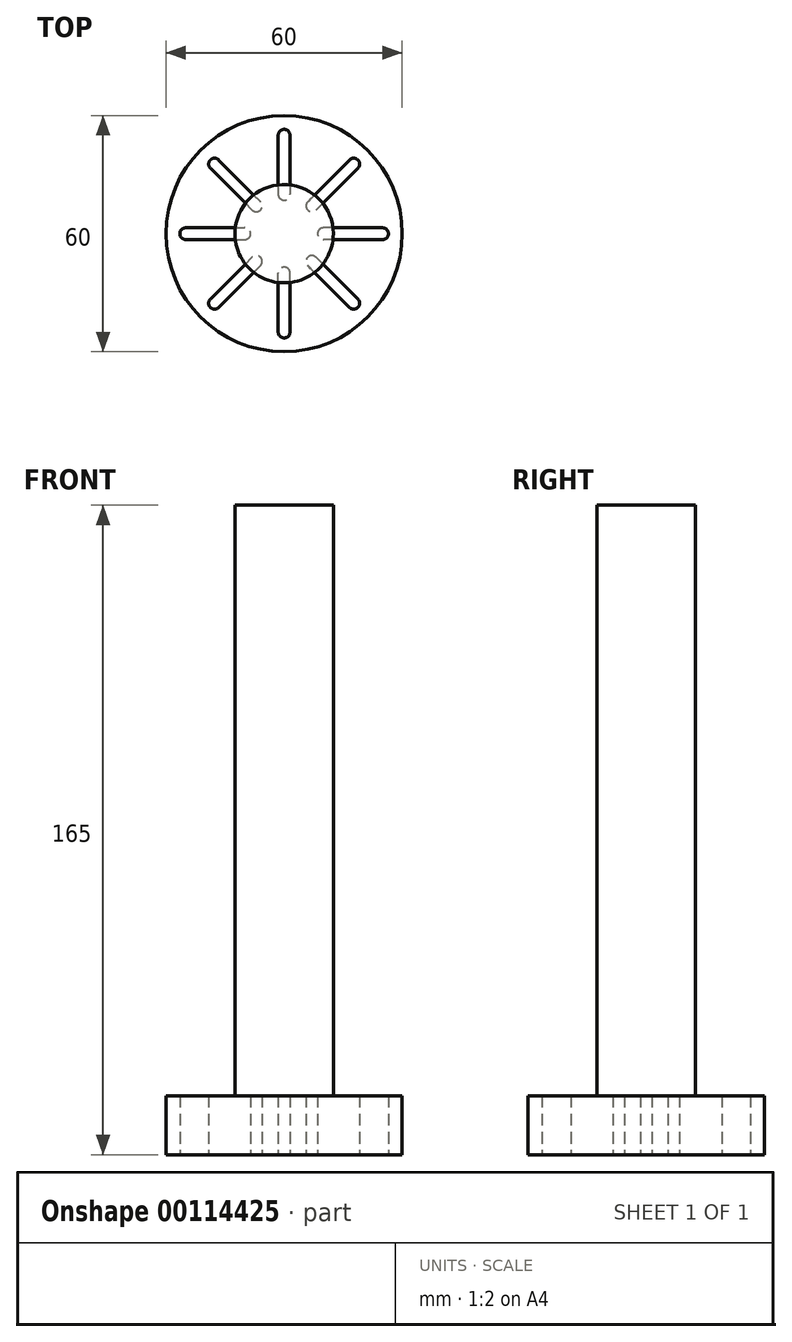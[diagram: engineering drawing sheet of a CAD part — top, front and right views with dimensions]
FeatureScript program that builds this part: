
annotation { "Feature Type Name" : "Feature", "Feature Type Description" : "" }
export const myFeature = defineFeature(function(context is Context, id is Id, definition is map)
    precondition{}
    {
        {
            var Q0;
            Q0=qCreatedBy(makeId("Top.planeOp"),FACE);
            var sketch = newSketch(context, id + "F0", { "sketchPlane" : qUnion([Q0])});
            skCircle(sketch, "E0", {"center": v(0, 0) * mm, "radius": 30 * mm});
            skArc(sketch, "E1", {"start": v(-25, 1.5) * mm, "mid": v(-26.5, 0) * mm, "end": v(-25, -1.5) * mm});
            skLineSegment(sketch, "E2.bottom", {"start": v(-25, 1.5) * mm, "end": v(-10, 1.5) * mm});
            skLineSegment(sketch, "E2.top", {"start": v(-25, -1.5) * mm, "end": v(-10, -1.5) * mm});
            skLineSegment(sketch, "E2.left", {"start": v(-25, 1.5) * mm, "end": v(-25, -1.5) * mm, "construction": true});
            skLineSegment(sketch, "E2.right", {"start": v(-10, 1.5) * mm, "end": v(-10, -1.5) * mm, "construction": true});
            skArc(sketch, "E3", {"start": v(-10, -1.5) * mm, "mid": v(-8.5, 0) * mm, "end": v(-10, 1.5) * mm});
            skLineSegment(sketch, "E4.1.0", {"start": v(-18.74, -16.62) * mm, "end": v(-8.13, -6.01) * mm});
            skLineSegment(sketch, "E4.1.1", {"start": v(-16.62, -18.74) * mm, "end": v(-6.01, -8.13) * mm});
            skArc(sketch, "E4.1.2", {"start": v(-6.01, -8.13) * mm, "mid": v(-6.01, -6.01) * mm, "end": v(-8.13, -6.01) * mm});
            skArc(sketch, "E4.1.3", {"start": v(-18.74, -16.62) * mm, "mid": v(-18.74, -18.74) * mm, "end": v(-16.62, -18.74) * mm});
            skLineSegment(sketch, "E4.2.0", {"start": v(-1.5, -25) * mm, "end": v(-1.5, -10) * mm});
            skLineSegment(sketch, "E4.2.1", {"start": v(1.5, -25) * mm, "end": v(1.5, -10) * mm});
            skArc(sketch, "E4.2.2", {"start": v(1.5, -10) * mm, "mid": v(0, -8.5) * mm, "end": v(-1.5, -10) * mm});
            skArc(sketch, "E4.2.3", {"start": v(-1.5, -25) * mm, "mid": v(0, -26.5) * mm, "end": v(1.5, -25) * mm});
            skLineSegment(sketch, "E4.3.0", {"start": v(16.62, -18.74) * mm, "end": v(6.01, -8.13) * mm});
            skLineSegment(sketch, "E4.3.1", {"start": v(18.74, -16.62) * mm, "end": v(8.13, -6.01) * mm});
            skArc(sketch, "E4.3.2", {"start": v(8.13, -6.01) * mm, "mid": v(6.01, -6.01) * mm, "end": v(6.01, -8.13) * mm});
            skArc(sketch, "E4.3.3", {"start": v(16.62, -18.74) * mm, "mid": v(18.74, -18.74) * mm, "end": v(18.74, -16.62) * mm});
            skLineSegment(sketch, "E4.4.0", {"start": v(25, -1.5) * mm, "end": v(10, -1.5) * mm});
            skLineSegment(sketch, "E4.4.1", {"start": v(25, 1.5) * mm, "end": v(10, 1.5) * mm});
            skArc(sketch, "E4.4.2", {"start": v(10, 1.5) * mm, "mid": v(8.5, 0) * mm, "end": v(10, -1.5) * mm});
            skArc(sketch, "E4.4.3", {"start": v(25, -1.5) * mm, "mid": v(26.5, 0) * mm, "end": v(25, 1.5) * mm});
            skLineSegment(sketch, "E4.5.0", {"start": v(18.74, 16.62) * mm, "end": v(8.13, 6.01) * mm});
            skLineSegment(sketch, "E4.5.1", {"start": v(16.62, 18.74) * mm, "end": v(6.01, 8.13) * mm});
            skArc(sketch, "E4.5.2", {"start": v(6.01, 8.13) * mm, "mid": v(6.01, 6.01) * mm, "end": v(8.13, 6.01) * mm});
            skArc(sketch, "E4.5.3", {"start": v(18.74, 16.62) * mm, "mid": v(18.74, 18.74) * mm, "end": v(16.62, 18.74) * mm});
            skLineSegment(sketch, "E4.6.0", {"start": v(1.5, 25) * mm, "end": v(1.5, 10) * mm});
            skLineSegment(sketch, "E4.6.1", {"start": v(-1.5, 25) * mm, "end": v(-1.5, 10) * mm});
            skArc(sketch, "E4.6.2", {"start": v(-1.5, 10) * mm, "mid": v(0, 8.5) * mm, "end": v(1.5, 10) * mm});
            skArc(sketch, "E4.6.3", {"start": v(1.5, 25) * mm, "mid": v(0, 26.5) * mm, "end": v(-1.5, 25) * mm});
            skLineSegment(sketch, "E4.7.0", {"start": v(-16.62, 18.74) * mm, "end": v(-6.01, 8.13) * mm});
            skLineSegment(sketch, "E4.7.1", {"start": v(-18.74, 16.62) * mm, "end": v(-8.13, 6.01) * mm});
            skArc(sketch, "E4.7.2", {"start": v(-8.13, 6.01) * mm, "mid": v(-6.01, 6.01) * mm, "end": v(-6.01, 8.13) * mm});
            skArc(sketch, "E4.7.3", {"start": v(-16.62, 18.74) * mm, "mid": v(-18.74, 18.74) * mm, "end": v(-18.74, 16.62) * mm});
            skSolve(sketch);
        }
        {
            var Q0;
            Q0=makeQuery(id+"F0.imprint","IMPRINT",FACE,{"disambiguationData":[TD([[makeQuery(id+"F0.imprint","IMPRINT",EDGE,{"derivedFrom":sQuery(id+"F0.wireOp",EDGE,"E0")}),1.0]])]});
            extrude(context, id + "F1", {"entities" : qUnion([Q0]), "depth" : 15 * mm});
        }
        {
            var Q0;
            Q0=makeQuery(id+"F1.opExtrude","CAP_FACE",FACE,{"disambiguationData":[OSD([sQuery(id+"F0.wireOp",EDGE,"E0"),sQuery(id+"F0.wireOp",EDGE,"E1"),sQuery(id+"F0.wireOp",EDGE,"E2.bottom"),sQuery(id+"F0.wireOp",EDGE,"E2.top"),sQuery(id+"F0.wireOp",EDGE,"E3"),sQuery(id+"F0.wireOp",EDGE,"E4.1.0"),sQuery(id+"F0.wireOp",EDGE,"E4.1.1"),sQuery(id+"F0.wireOp",EDGE,"E4.1.2"),sQuery(id+"F0.wireOp",EDGE,"E4.1.3"),sQuery(id+"F0.wireOp",EDGE,"E4.2.0"),sQuery(id+"F0.wireOp",EDGE,"E4.2.1"),sQuery(id+"F0.wireOp",EDGE,"E4.2.2"),sQuery(id+"F0.wireOp",EDGE,"E4.2.3"),sQuery(id+"F0.wireOp",EDGE,"E4.3.0"),sQuery(id+"F0.wireOp",EDGE,"E4.3.1"),sQuery(id+"F0.wireOp",EDGE,"E4.3.2"),sQuery(id+"F0.wireOp",EDGE,"E4.3.3"),sQuery(id+"F0.wireOp",EDGE,"E4.4.0"),sQuery(id+"F0.wireOp",EDGE,"E4.4.1"),sQuery(id+"F0.wireOp",EDGE,"E4.4.2"),sQuery(id+"F0.wireOp",EDGE,"E4.4.3"),sQuery(id+"F0.wireOp",EDGE,"E4.5.0"),sQuery(id+"F0.wireOp",EDGE,"E4.5.1"),sQuery(id+"F0.wireOp",EDGE,"E4.5.2"),sQuery(id+"F0.wireOp",EDGE,"E4.5.3"),sQuery(id+"F0.wireOp",EDGE,"E4.6.0"),sQuery(id+"F0.wireOp",EDGE,"E4.6.1"),sQuery(id+"F0.wireOp",EDGE,"E4.6.2"),sQuery(id+"F0.wireOp",EDGE,"E4.6.3"),sQuery(id+"F0.wireOp",EDGE,"E4.7.0"),sQuery(id+"F0.wireOp",EDGE,"E4.7.1"),sQuery(id+"F0.wireOp",EDGE,"E4.7.2"),sQuery(id+"F0.wireOp",EDGE,"E4.7.3")])],"isStart":false});
            var sketch = newSketch(context, id + "F2", { "sketchPlane" : qUnion([Q0])});
            skCircle(sketch, "E5", {"center": v(0, 0) * mm, "radius": 12.5 * mm});
            skSolve(sketch);
        }
        {
            var Q0;
            {var subQ14=makeQuery(id+"F1.opExtrude","CAP_EDGE",EDGE,{"disambiguationData":[OSD([sQuery(id+"F0.wireOp",EDGE,"E3")])],"isStart":false});Q0=makeQuery(id+"F2.imprint","IMPRINT",FACE,{"disambiguationData":[TD([[makeQuery(id+"F2.imprint","IMPRINT",EDGE,{"derivedFrom":subQ14}),-1.0]])]});}
            var Q1;
            {var subQ5=makeQuery(id+"F1.opExtrude","CAP_EDGE",EDGE,{"disambiguationData":[OSD([sQuery(id+"F0.wireOp",EDGE,"E3")])],"isStart":false});Q1=makeQuery(id+"F2.imprint","IMPRINT",FACE,{"disambiguationData":[TD([[makeQuery(id+"F2.imprint","IMPRINT",EDGE,{"derivedFrom":subQ5}),1.0]])]});}
            var Q2;
            {var subQ5=makeQuery(id+"F1.opExtrude","CAP_EDGE",EDGE,{"disambiguationData":[OSD([sQuery(id+"F0.wireOp",EDGE,"E4.7.2")])],"isStart":false});Q2=makeQuery(id+"F2.imprint","IMPRINT",FACE,{"disambiguationData":[TD([[makeQuery(id+"F2.imprint","IMPRINT",EDGE,{"derivedFrom":subQ5}),1.0]])]});}
            var Q3;
            {var subQ5=makeQuery(id+"F1.opExtrude","CAP_EDGE",EDGE,{"disambiguationData":[OSD([sQuery(id+"F0.wireOp",EDGE,"E4.6.2")])],"isStart":false});Q3=makeQuery(id+"F2.imprint","IMPRINT",FACE,{"disambiguationData":[TD([[makeQuery(id+"F2.imprint","IMPRINT",EDGE,{"derivedFrom":subQ5}),1.0]])]});}
            var Q4;
            {var subQ5=makeQuery(id+"F1.opExtrude","CAP_EDGE",EDGE,{"disambiguationData":[OSD([sQuery(id+"F0.wireOp",EDGE,"E4.5.2")])],"isStart":false});Q4=makeQuery(id+"F2.imprint","IMPRINT",FACE,{"disambiguationData":[TD([[makeQuery(id+"F2.imprint","IMPRINT",EDGE,{"derivedFrom":subQ5}),1.0]])]});}
            var Q5;
            {var subQ5=makeQuery(id+"F1.opExtrude","CAP_EDGE",EDGE,{"disambiguationData":[OSD([sQuery(id+"F0.wireOp",EDGE,"E4.4.2")])],"isStart":false});Q5=makeQuery(id+"F2.imprint","IMPRINT",FACE,{"disambiguationData":[TD([[makeQuery(id+"F2.imprint","IMPRINT",EDGE,{"derivedFrom":subQ5}),1.0]])]});}
            var Q6;
            {var subQ5=makeQuery(id+"F1.opExtrude","CAP_EDGE",EDGE,{"disambiguationData":[OSD([sQuery(id+"F0.wireOp",EDGE,"E4.3.2")])],"isStart":false});Q6=makeQuery(id+"F2.imprint","IMPRINT",FACE,{"disambiguationData":[TD([[makeQuery(id+"F2.imprint","IMPRINT",EDGE,{"derivedFrom":subQ5}),1.0]])]});}
            var Q7;
            {var subQ5=makeQuery(id+"F1.opExtrude","CAP_EDGE",EDGE,{"disambiguationData":[OSD([sQuery(id+"F0.wireOp",EDGE,"E4.2.2")])],"isStart":false});Q7=makeQuery(id+"F2.imprint","IMPRINT",FACE,{"disambiguationData":[TD([[makeQuery(id+"F2.imprint","IMPRINT",EDGE,{"derivedFrom":subQ5}),1.0]])]});}
            var Q8;
            {var subQ5=makeQuery(id+"F1.opExtrude","CAP_EDGE",EDGE,{"disambiguationData":[OSD([sQuery(id+"F0.wireOp",EDGE,"E4.1.2")])],"isStart":false});Q8=makeQuery(id+"F2.imprint","IMPRINT",FACE,{"disambiguationData":[TD([[makeQuery(id+"F2.imprint","IMPRINT",EDGE,{"derivedFrom":subQ5}),1.0]])]});}
            extrude(context, id + "F3", {"entities" : qUnion([Q0, Q1, Q2, Q3, Q4, Q5, Q6, Q7, Q8]), "operationType" : NewBodyOperationType.ADD, "depth" : 150 * mm});
        }
    });
